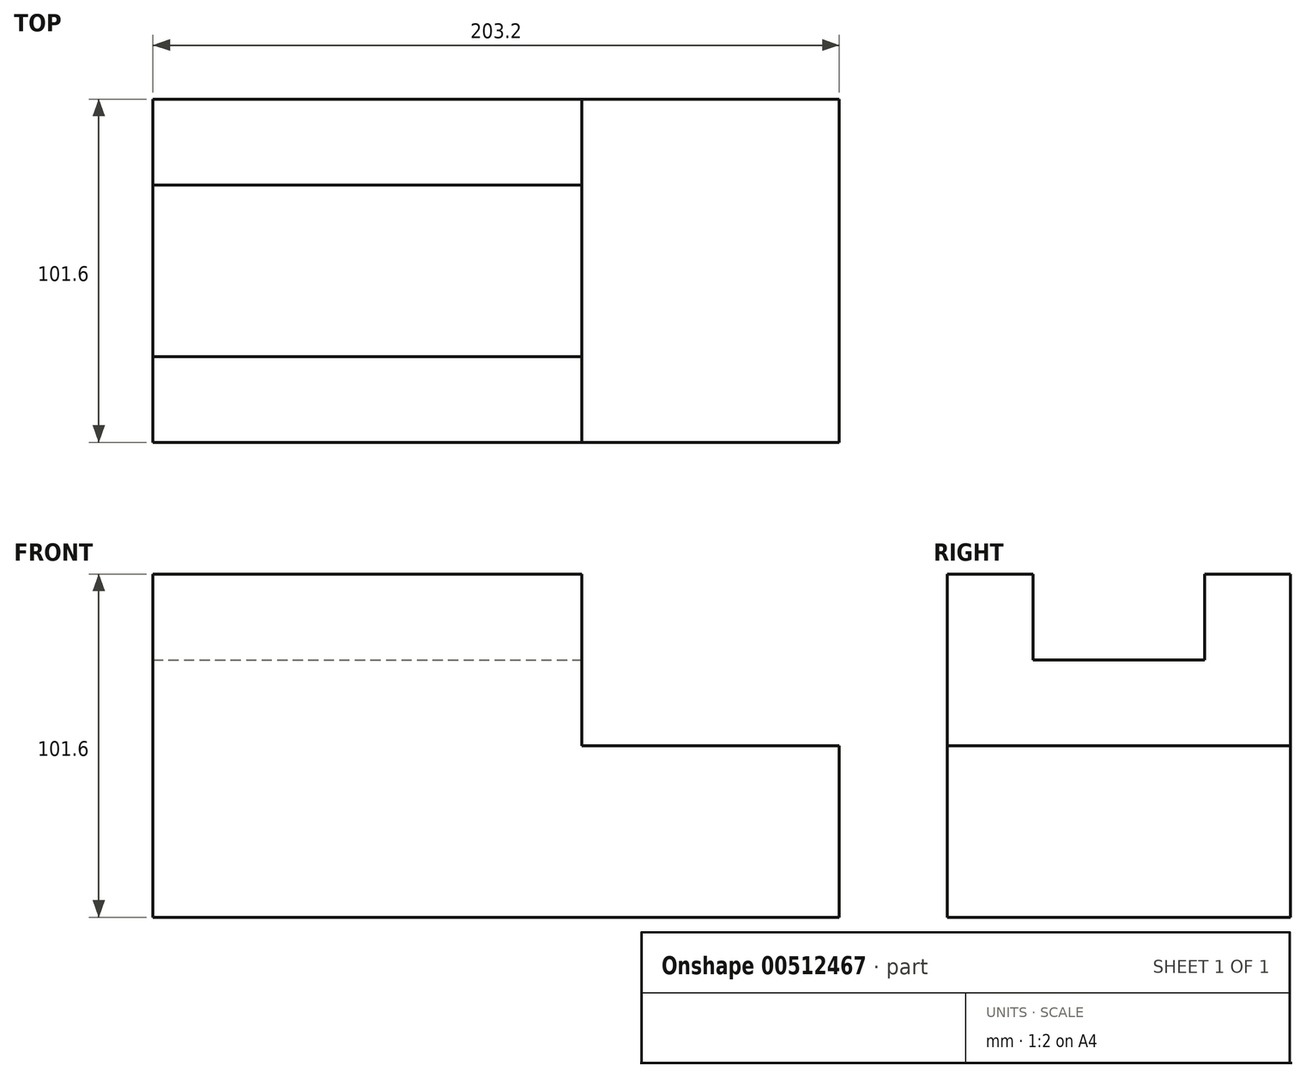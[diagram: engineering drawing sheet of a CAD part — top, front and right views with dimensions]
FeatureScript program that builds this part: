
annotation { "Feature Type Name" : "Feature", "Feature Type Description" : "" }
export const myFeature = defineFeature(function(context is Context, id is Id, definition is map)
    precondition{}
    {
        {
            var Q0;
            Q0=qCreatedBy(makeId("Front.planeOp"),FACE);
            var sketch = newSketch(context, id + "F0", { "sketchPlane" : qUnion([Q0])});
            skLineSegment(sketch, "E0.bottom", {"start": v(0, 0) * mm, "end": v(203.2, 0) * mm});
            skLineSegment(sketch, "E0.top", {"start": v(0, 50.8) * mm, "end": v(203.2, 50.8) * mm});
            skLineSegment(sketch, "E0.left", {"start": v(0, 0) * mm, "end": v(0, 50.8) * mm});
            skLineSegment(sketch, "E0.right", {"start": v(203.2, 0) * mm, "end": v(203.2, 50.8) * mm});
            skSolve(sketch);
        }
        {
            var Q0;
            Q0=makeQuery(id+"F0.imprint","IMPRINT",FACE,{"disambiguationData":[TD([[makeQuery(id+"F0.imprint","IMPRINT",EDGE,{"derivedFrom":sQuery(id+"F0.wireOp",EDGE,"E0.bottom")}),1.0]])]});
            extrude(context, id + "F1", {"entities" : qUnion([Q0]), "depth" : 101.6 * mm});
        }
        {
            var Q0;
            Q0=makeQuery(id+"F1.opExtrude","SWEPT_FACE",FACE,{"disambiguationData":[OSD([sQuery(id+"F0.wireOp",EDGE,"E0.top")])]});
            var sketch = newSketch(context, id + "F2", { "sketchPlane" : qUnion([Q0])});
            skLineSegment(sketch, "E1.bottom", {"start": v(0, 0) * mm, "end": v(127, 0) * mm});
            skLineSegment(sketch, "E1.top", {"start": v(0, -101.6) * mm, "end": v(127, -101.6) * mm});
            skLineSegment(sketch, "E1.left", {"start": v(0, 0) * mm, "end": v(0, -101.6) * mm});
            skLineSegment(sketch, "E1.right", {"start": v(127, 0) * mm, "end": v(127, -101.6) * mm});
            skSolve(sketch);
        }
        {
            var Q0;
            Q0=makeQuery(id+"F2.imprint","IMPRINT",FACE,{"disambiguationData":[TD([[makeQuery(id+"F2.imprint","IMPRINT",EDGE,{"derivedFrom":sQuery(id+"F2.wireOp",EDGE,"E1.bottom")}),-1.0]])]});
            extrude(context, id + "F3", {"entities" : qUnion([Q0]), "operationType" : NewBodyOperationType.ADD, "depth" : 25.4 * mm});
        }
        {
            var Q0;
            Q0=makeQuery(id+"F3.opExtrude","CAP_FACE",FACE,{"disambiguationData":[OSD([sQuery(id+"F2.wireOp",EDGE,"E1.bottom"),sQuery(id+"F2.wireOp",EDGE,"E1.top"),sQuery(id+"F2.wireOp",EDGE,"E1.left"),sQuery(id+"F2.wireOp",EDGE,"E1.right")])],"isStart":false});
            var sketch = newSketch(context, id + "F4", { "sketchPlane" : qUnion([Q0])});
            skLineSegment(sketch, "E2.bottom", {"start": v(0, 0) * mm, "end": v(127, 0) * mm});
            skLineSegment(sketch, "E2.top", {"start": v(0, -25.4) * mm, "end": v(127, -25.4) * mm});
            skLineSegment(sketch, "E2.left", {"start": v(0, 0) * mm, "end": v(0, -25.4) * mm});
            skLineSegment(sketch, "E2.right", {"start": v(127, 0) * mm, "end": v(127, -25.4) * mm});
            skSolve(sketch);
        }
        {
            var Q0;
            Q0=makeQuery(id+"F4.imprint","IMPRINT",FACE,{"disambiguationData":[TD([[makeQuery(id+"F4.imprint","IMPRINT",EDGE,{"derivedFrom":sQuery(id+"F4.wireOp",EDGE,"E2.bottom")}),-1.0]])]});
            extrude(context, id + "F5", {"entities" : qUnion([Q0]), "operationType" : NewBodyOperationType.ADD, "depth" : 25.4 * mm});
        }
        {
            var Q0;
            Q0=makeQuery(id+"F3.opExtrude","CAP_FACE",FACE,{"disambiguationData":[OSD([sQuery(id+"F2.wireOp",EDGE,"E1.bottom"),sQuery(id+"F2.wireOp",EDGE,"E1.top"),sQuery(id+"F2.wireOp",EDGE,"E1.left"),sQuery(id+"F2.wireOp",EDGE,"E1.right")])],"isStart":false});
            var sketch = newSketch(context, id + "F6", { "sketchPlane" : qUnion([Q0])});
            skLineSegment(sketch, "E3.bottom", {"start": v(0, -101.6) * mm, "end": v(127, -101.6) * mm});
            skLineSegment(sketch, "E3.top", {"start": v(0, -76.2) * mm, "end": v(127, -76.2) * mm});
            skLineSegment(sketch, "E3.left", {"start": v(0, -101.6) * mm, "end": v(0, -76.2) * mm});
            skLineSegment(sketch, "E3.right", {"start": v(127, -101.6) * mm, "end": v(127, -76.2) * mm});
            skSolve(sketch);
        }
        {
            var Q0;
            Q0=makeQuery(id+"F6.imprint","IMPRINT",FACE,{"disambiguationData":[TD([[makeQuery(id+"F6.imprint","IMPRINT",EDGE,{"derivedFrom":sQuery(id+"F6.wireOp",EDGE,"E3.bottom")}),1.0]])]});
            extrude(context, id + "F7", {"entities" : qUnion([Q0]), "operationType" : NewBodyOperationType.ADD, "depth" : 25.4 * mm});
        }
    });
